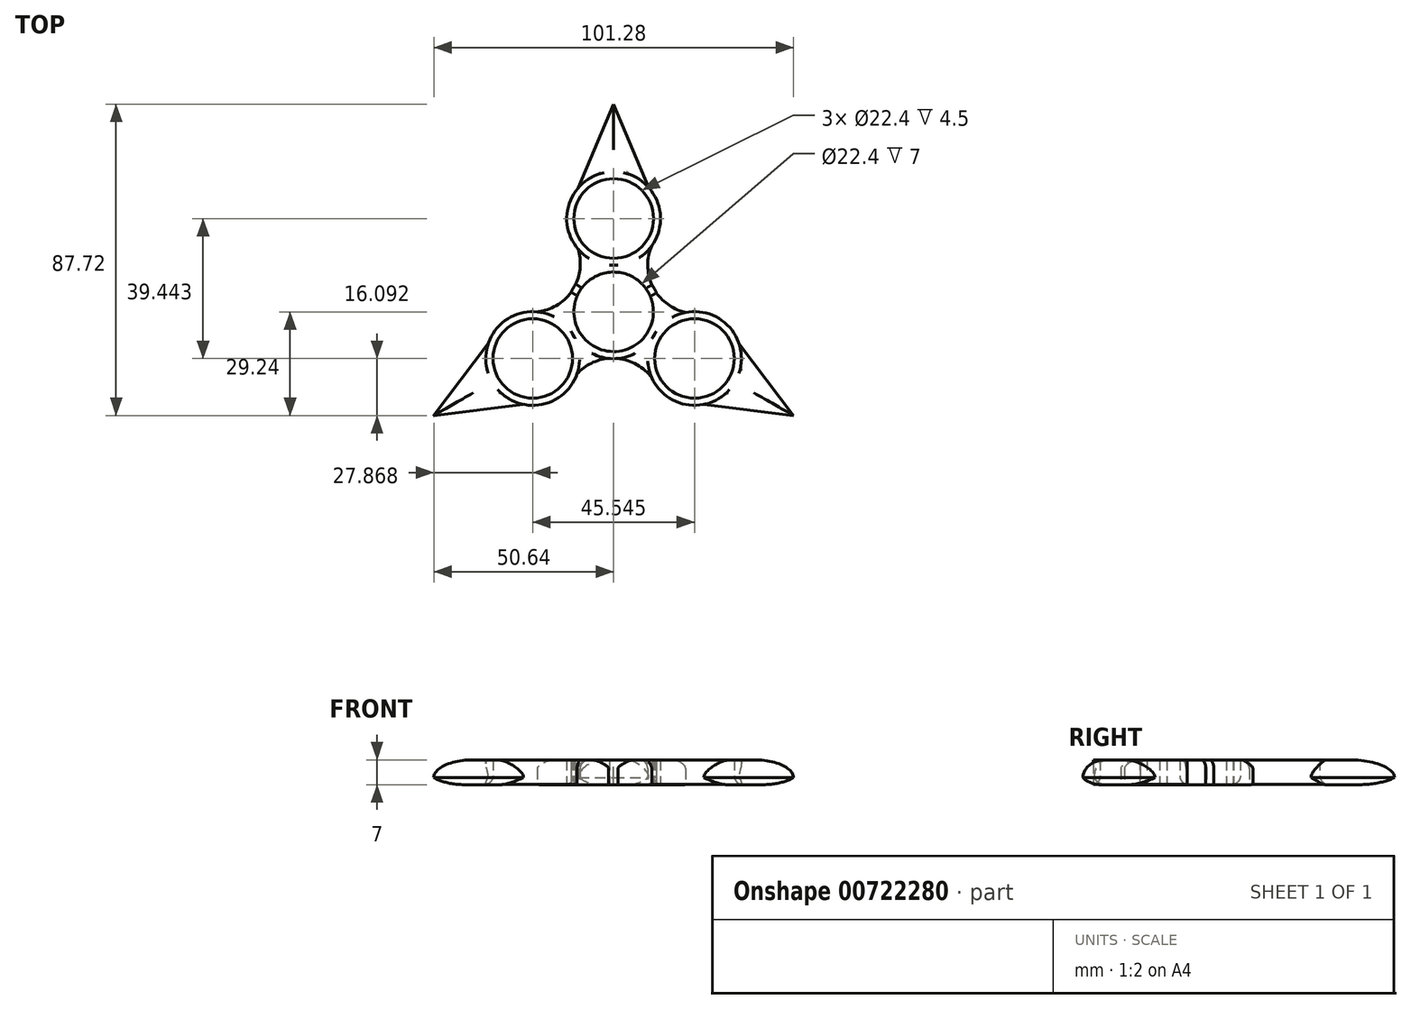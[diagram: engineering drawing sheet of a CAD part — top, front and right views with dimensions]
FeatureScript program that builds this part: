
annotation { "Feature Type Name" : "Feature", "Feature Type Description" : "" }
export const myFeature = defineFeature(function(context is Context, id is Id, definition is map)
    precondition{}
    {
        {
            var Q0;
            Q0=qCreatedBy(makeId("Top.planeOp"),FACE);
            var sketch = newSketch(context, id + "F0", { "sketchPlane" : qUnion([Q0])});
            skCircle(sketch, "E0", {"center": v(0, 0) * mm, "radius": 11.2 * mm});
            skCircle(sketch, "E1", {"center": v(0, 0) * mm, "radius": 13.2 * mm});
            skCircle(sketch, "E2", {"center": v(0, 26.3) * mm, "radius": 11.2 * mm});
            skCircle(sketch, "E3", {"center": v(0, 26.3) * mm, "radius": 13.2 * mm});
            skCircle(sketch, "E4.1.0", {"center": v(-22.77, -13.15) * mm, "radius": 13.2 * mm});
            skCircle(sketch, "E4.1.1", {"center": v(-22.77, -13.15) * mm, "radius": 11.2 * mm});
            skCircle(sketch, "E4.2.0", {"center": v(22.77, -13.15) * mm, "radius": 13.2 * mm});
            skCircle(sketch, "E4.2.1", {"center": v(22.77, -13.15) * mm, "radius": 11.2 * mm});
            skArc(sketch, "E5", {"start": v(10.74, 18.62) * mm, "mid": v(11.1, 6.97) * mm, "end": v(20.3, -0.18) * mm});
            skArc(sketch, "E6.1.0", {"start": v(-21.5, 0) * mm, "mid": v(-11.58, 6.12) * mm, "end": v(-10, 17.67) * mm});
            skArc(sketch, "E6.2.0", {"start": v(10.76, -18.61) * mm, "mid": v(0.49, -13.1) * mm, "end": v(-10.3, -17.5) * mm});
            skLineSegment(sketch, "E7", {"start": v(-9.9, 35.03) * mm, "end": v(0, 58.48) * mm});
            skLineSegment(sketch, "E8", {"start": v(0, 58.48) * mm, "end": v(9.9, 35.03) * mm});
            skLineSegment(sketch, "E9.1.0", {"start": v(-50.64, -29.24) * mm, "end": v(-35.29, -8.95) * mm});
            skLineSegment(sketch, "E9.1.1", {"start": v(-25.4, -26.08) * mm, "end": v(-50.64, -29.24) * mm});
            skLineSegment(sketch, "E9.2.0", {"start": v(50.64, -29.24) * mm, "end": v(25.4, -26.08) * mm});
            skLineSegment(sketch, "E9.2.1", {"start": v(35.29, -8.95) * mm, "end": v(50.64, -29.24) * mm});
            skSolve(sketch);
        }
        {
            var Q0;
            Q0=qSketchRegion(id+"F0",true);
            extrude(context, id + "F1", {"entities" : qUnion([Q0]), "depth" : 7 * mm, "offsetDistance" : 25 * mm});
        }
        {
            var Q0;
            {var subQ0=sQuery(id+"F0.wireOp",EDGE,"E6.2.0");Q0=makeQuery(id+"F1.opExtrude","CAP_EDGE",EDGE,{"disambiguationData":[OSD([subQ0]),TDD([makeQuery(id+"F0.imprint","IMPRINT",EDGE,{"disambiguationData":[TD([[makeQuery(id+"F0.imprint","INTERSECT",VERTEX,{"derivedFrom":[sQuery(id+"F0.wireOp",EDGE,"E4.2.0"),subQ0]}),-1.0]])],"derivedFrom":subQ0})])],"isStart":false});}
            var Q1;
            {var subQ0=sQuery(id+"F0.wireOp",EDGE,"E6.2.0");Q1=makeQuery(id+"F1.opExtrude","CAP_EDGE",EDGE,{"disambiguationData":[OSD([subQ0]),TDD([makeQuery(id+"F0.imprint","IMPRINT",EDGE,{"disambiguationData":[TD([[makeQuery(id+"F0.imprint","INTERSECT",VERTEX,{"derivedFrom":[sQuery(id+"F0.wireOp",EDGE,"E4.1.0"),subQ0]}),1.0]])],"derivedFrom":subQ0})])],"isStart":false});}
            var Q2;
            {var subQ0=sQuery(id+"F0.wireOp",EDGE,"E6.1.0");Q2=makeQuery(id+"F1.opExtrude","CAP_EDGE",EDGE,{"disambiguationData":[OSD([subQ0]),TDD([makeQuery(id+"F0.imprint","IMPRINT",EDGE,{"disambiguationData":[TD([[makeQuery(id+"F0.imprint","INTERSECT",VERTEX,{"derivedFrom":[sQuery(id+"F0.wireOp",EDGE,"E3"),subQ0]}),1.0]])],"derivedFrom":subQ0})])],"isStart":false});}
            var Q3;
            {var subQ0=sQuery(id+"F0.wireOp",EDGE,"E6.1.0");var subQ1=sQuery(id+"F0.wireOp",EDGE,"E1");Q3=makeQuery(id+"F1.opExtrude","CAP_EDGE",EDGE,{"disambiguationData":[OSD([subQ1]),TDD([makeQuery(id+"F0.imprint","IMPRINT",EDGE,{"disambiguationData":[TD([[makeQuery(id+"F0.imprint","INTERSECT",VERTEX,{"disambiguationData":[OD(0.0)],"derivedFrom":[subQ1,subQ0]}),-1.0]])],"derivedFrom":subQ1})])],"isStart":false});}
            var Q4;
            {var subQ0=sQuery(id+"F0.wireOp",EDGE,"E6.1.0");Q4=makeQuery(id+"F1.opExtrude","CAP_EDGE",EDGE,{"disambiguationData":[OSD([subQ0]),TDD([makeQuery(id+"F0.imprint","IMPRINT",EDGE,{"disambiguationData":[TD([[makeQuery(id+"F0.imprint","INTERSECT",VERTEX,{"derivedFrom":[sQuery(id+"F0.wireOp",EDGE,"E4.1.0"),subQ0]}),-1.0]])],"derivedFrom":subQ0})])],"isStart":false});}
            var Q5;
            {var subQ0=sQuery(id+"F0.wireOp",EDGE,"E5");Q5=makeQuery(id+"F1.opExtrude","CAP_EDGE",EDGE,{"disambiguationData":[OSD([subQ0]),TDD([makeQuery(id+"F0.imprint","IMPRINT",EDGE,{"disambiguationData":[TD([[makeQuery(id+"F0.imprint","INTERSECT",VERTEX,{"derivedFrom":[sQuery(id+"F0.wireOp",EDGE,"E3"),subQ0]}),-1.0]])],"derivedFrom":subQ0})])],"isStart":false});}
            var Q6;
            {var subQ0=sQuery(id+"F0.wireOp",EDGE,"E5");var subQ1=sQuery(id+"F0.wireOp",EDGE,"E1");Q6=makeQuery(id+"F1.opExtrude","CAP_EDGE",EDGE,{"disambiguationData":[OSD([subQ1]),TDD([makeQuery(id+"F0.imprint","IMPRINT",EDGE,{"disambiguationData":[TD([[makeQuery(id+"F0.imprint","INTERSECT",VERTEX,{"disambiguationData":[OD(0.0)],"derivedFrom":[subQ1,subQ0]}),1.0]])],"derivedFrom":subQ1})])],"isStart":false});}
            var Q7;
            {var subQ0=sQuery(id+"F0.wireOp",EDGE,"E5");Q7=makeQuery(id+"F1.opExtrude","CAP_EDGE",EDGE,{"disambiguationData":[OSD([subQ0]),TDD([makeQuery(id+"F0.imprint","IMPRINT",EDGE,{"disambiguationData":[TD([[makeQuery(id+"F0.imprint","INTERSECT",VERTEX,{"derivedFrom":[sQuery(id+"F0.wireOp",EDGE,"E4.2.0"),subQ0]}),1.0]])],"derivedFrom":subQ0})])],"isStart":false});}
            var Q8;
            Q8=makeQuery(id+"F1.opExtrude","CAP_EDGE",EDGE,{"disambiguationData":[OSD([sQuery(id+"F0.wireOp",EDGE,"E4.1.1")])],"isStart":true});
            var Q9;
            Q9=makeQuery(id+"F1.opExtrude","CAP_EDGE",EDGE,{"disambiguationData":[OSD([sQuery(id+"F0.wireOp",EDGE,"E4.2.1")])],"isStart":true});
            var Q10;
            Q10=makeQuery(id+"F1.opExtrude","CAP_EDGE",EDGE,{"disambiguationData":[OSD([sQuery(id+"F0.wireOp",EDGE,"E2")])],"isStart":true});
            fillet(context, id + "F2", {"entities" : qUnion([Q0, Q1, Q2, Q3, Q4, Q5, Q6, Q7, Q8, Q9, Q10]), "radius" : 2.5 * mm, "tangentPropagation" : true, "allowEdgeOverflow" : false});
        }
        {
            var Q0;
            Q0=makeQuery(id+"F1.opExtrude","CAP_EDGE",EDGE,{"disambiguationData":[OSD([sQuery(id+"F0.wireOp",EDGE,"E9.1.0")])],"isStart":false});
            var Q1;
            Q1=makeQuery(id+"F1.opExtrude","CAP_EDGE",EDGE,{"disambiguationData":[OSD([sQuery(id+"F0.wireOp",EDGE,"E9.1.1")])],"isStart":false});
            var Q2;
            Q2=makeQuery(id+"F1.opExtrude","CAP_EDGE",EDGE,{"disambiguationData":[OSD([sQuery(id+"F0.wireOp",EDGE,"E9.2.0")])],"isStart":false});
            var Q3;
            Q3=makeQuery(id+"F1.opExtrude","CAP_EDGE",EDGE,{"disambiguationData":[OSD([sQuery(id+"F0.wireOp",EDGE,"E9.2.1")])],"isStart":false});
            var Q4;
            Q4=makeQuery(id+"F1.opExtrude","CAP_EDGE",EDGE,{"disambiguationData":[OSD([sQuery(id+"F0.wireOp",EDGE,"E7")])],"isStart":false});
            var Q5;
            Q5=makeQuery(id+"F1.opExtrude","CAP_EDGE",EDGE,{"disambiguationData":[OSD([sQuery(id+"F0.wireOp",EDGE,"E8")])],"isStart":false});
            fillet(context, id + "F3", {"entities" : qUnion([Q0, Q1, Q2, Q3, Q4, Q5]), "radius" : 5 * mm, "tangentPropagation" : true, "allowEdgeOverflow" : false});
        }
        {
            var Q0;
            Q0=makeQuery(id+"F1.opExtrude","CAP_EDGE",EDGE,{"disambiguationData":[OSD([sQuery(id+"F0.wireOp",EDGE,"E8")])],"isStart":true});
            var Q1;
            Q1=makeQuery(id+"F1.opExtrude","CAP_EDGE",EDGE,{"disambiguationData":[OSD([sQuery(id+"F0.wireOp",EDGE,"E7")])],"isStart":true});
            var Q2;
            Q2=makeQuery(id+"F1.opExtrude","CAP_EDGE",EDGE,{"disambiguationData":[OSD([sQuery(id+"F0.wireOp",EDGE,"E9.2.1")])],"isStart":true});
            var Q3;
            Q3=makeQuery(id+"F1.opExtrude","CAP_EDGE",EDGE,{"disambiguationData":[OSD([sQuery(id+"F0.wireOp",EDGE,"E9.1.1")])],"isStart":true});
            var Q4;
            Q4=makeQuery(id+"F1.opExtrude","CAP_EDGE",EDGE,{"disambiguationData":[OSD([sQuery(id+"F0.wireOp",EDGE,"E9.1.0")])],"isStart":true});
            fillet(context, id + "F4", {"entities" : qUnion([Q0, Q1, Q2, Q3, Q4]), "radius" : 5 * mm, "tangentPropagation" : true, "allowEdgeOverflow" : false});
        }
        {
            var Q0;
            Q0=makeQuery(id+"F1.opExtrude","CAP_EDGE",EDGE,{"disambiguationData":[OSD([sQuery(id+"F0.wireOp",EDGE,"E9.2.0")])],"isStart":true});
            fillet(context, id + "F5", {"entities" : qUnion([Q0]), "radius" : 5 * mm, "tangentPropagation" : true, "allowEdgeOverflow" : false});
        }
    });
